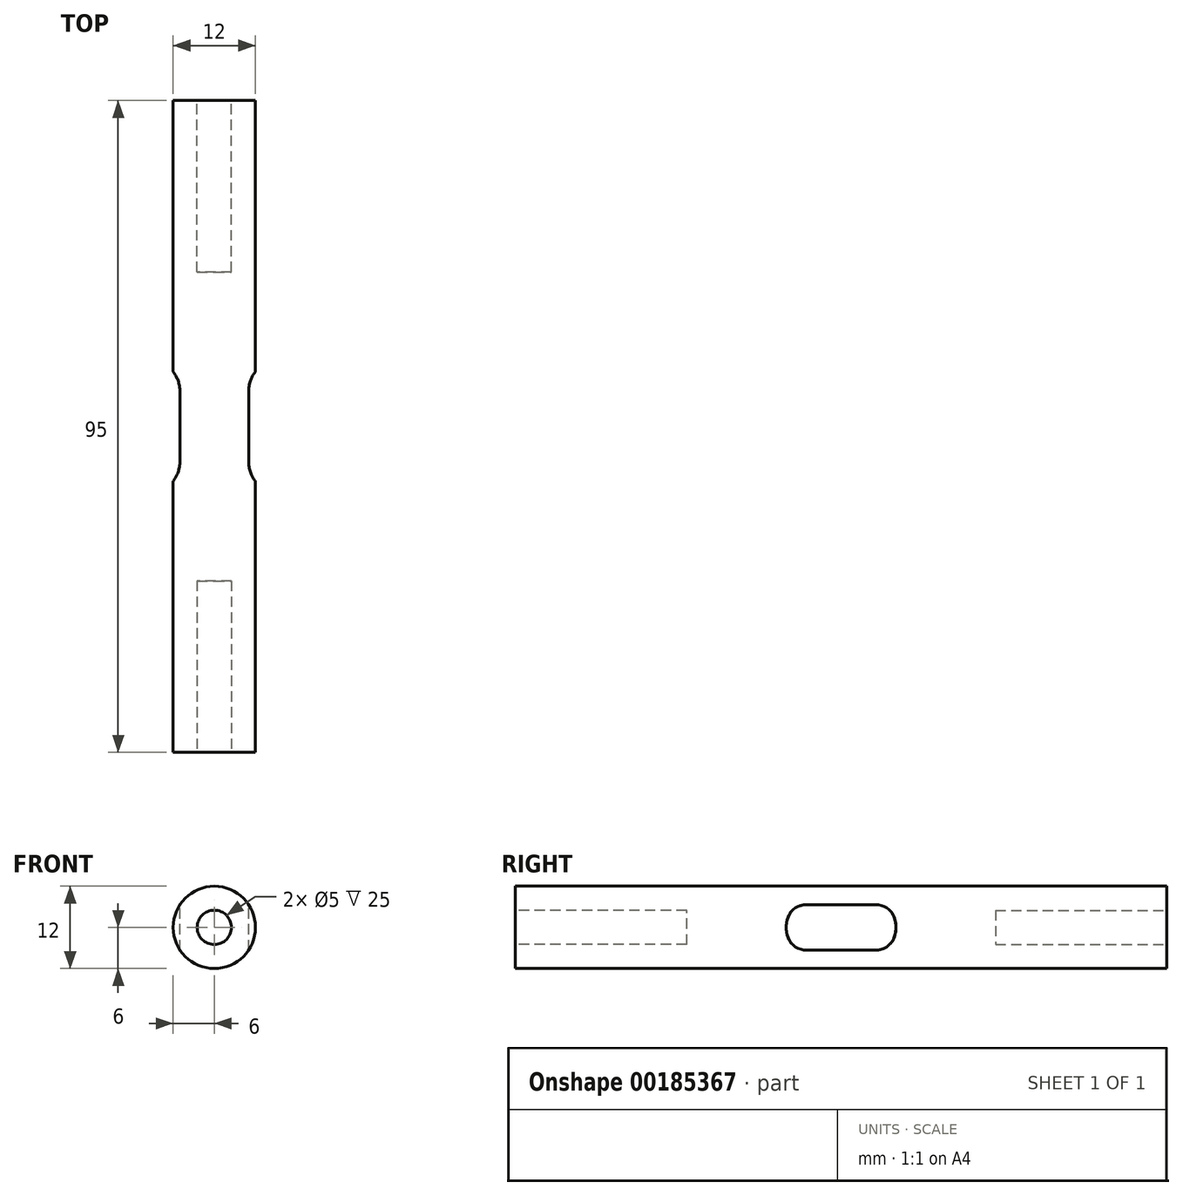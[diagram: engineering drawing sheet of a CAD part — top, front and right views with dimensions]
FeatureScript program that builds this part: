
annotation { "Feature Type Name" : "Feature", "Feature Type Description" : "" }
export const myFeature = defineFeature(function(context is Context, id is Id, definition is map)
    precondition{}
    {
        {
            var Q0;
            Q0=qCreatedBy(makeId("Front.planeOp"),FACE);
            var sketch = newSketch(context, id + "F0", { "sketchPlane" : qUnion([Q0])});
            skCircle(sketch, "E0", {"center": v(0, 0) * mm, "radius": 6 * mm});
            skSolve(sketch);
        }
        {
            var Q0;
            Q0=makeQuery(id+"F0.imprint","IMPRINT",FACE,{"disambiguationData":[TD([[makeQuery(id+"F0.imprint","IMPRINT",EDGE,{"derivedFrom":sQuery(id+"F0.wireOp",EDGE,"E0")}),1.0]])]});
            extrude(context, id + "F1", {"entities" : qUnion([Q0]), "depth" : 95 * mm});
        }
        {
            var Q0;
            Q0=makeQuery(id+"F1.opExtrude","CAP_FACE",FACE,{"disambiguationData":[OSD([sQuery(id+"F0.wireOp",EDGE,"E0")])],"isStart":true});
            var sketch = newSketch(context, id + "F2", { "sketchPlane" : qUnion([Q0])});
            skCircle(sketch, "E1", {"center": v(0, 0) * mm, "radius": 2.5 * mm});
            skSolve(sketch);
        }
        {
            var Q0;
            Q0=makeQuery(id+"F2.imprint","IMPRINT",FACE,{"disambiguationData":[TD([[makeQuery(id+"F2.imprint","IMPRINT",EDGE,{"derivedFrom":sQuery(id+"F2.wireOp",EDGE,"E1")}),1.0]])]});
            extrude(context, id + "F3", {"entities" : qUnion([Q0]), "operationType" : NewBodyOperationType.REMOVE, "oppositeDirection" : true, "depth" : 25 * mm});
        }
        {
            var Q0;
            Q0=makeQuery(id+"F1.opExtrude","CAP_FACE",FACE,{"disambiguationData":[OSD([sQuery(id+"F0.wireOp",EDGE,"E0")])],"isStart":false});
            var sketch = newSketch(context, id + "F4", { "sketchPlane" : qUnion([Q0])});
            skCircle(sketch, "E2", {"center": v(0, 0) * mm, "radius": 2.5 * mm});
            skSolve(sketch);
        }
        {
            var Q0;
            Q0=makeQuery(id+"F4.imprint","IMPRINT",FACE,{"disambiguationData":[TD([[makeQuery(id+"F4.imprint","IMPRINT",EDGE,{"derivedFrom":sQuery(id+"F4.wireOp",EDGE,"E2")}),1.0]])]});
            extrude(context, id + "F5", {"entities" : qUnion([Q0]), "operationType" : NewBodyOperationType.REMOVE, "oppositeDirection" : true, "depth" : 25 * mm});
        }
        {
            var Q0;
            Q0=qCreatedBy(makeId("Top.planeOp"),FACE);
            var sketch = newSketch(context, id + "F6", { "sketchPlane" : qUnion([Q0])});
            skLineSegment(sketch, "E3.bottom", {"start": v(10, -37.5) * mm, "end": v(11.65, -37.5) * mm});
            skLineSegment(sketch, "E3.top", {"start": v(10, -57.5) * mm, "end": v(11.65, -57.5) * mm});
            skLineSegment(sketch, "E3.left", {"start": v(5, -42.5) * mm, "end": v(5, -52.5) * mm});
            skLineSegment(sketch, "E3.right", {"start": v(11.65, -37.5) * mm, "end": v(11.65, -57.5) * mm});
            skPoint(sketch, "E4.visualSharp", {"position": v(5, -37.5) * mm});
            skArc(sketch, "E4.filletArc", {"start": v(10, -37.5) * mm, "mid": v(6.46, -38.96) * mm, "end": v(5, -42.5) * mm});
            skPoint(sketch, "E5.visualSharp", {"position": v(5, -57.5) * mm});
            skArc(sketch, "E5.filletArc", {"start": v(5, -52.5) * mm, "mid": v(6.46, -56.04) * mm, "end": v(10, -57.5) * mm});
            skLineSegment(sketch, "E6.MirrorCS", {"start": v(-10, -37.5) * mm, "end": v(-11.65, -37.5) * mm});
            skLineSegment(sketch, "E7.MirrorCS", {"start": v(-10, -57.5) * mm, "end": v(-11.65, -57.5) * mm});
            skArc(sketch, "E8.MirrorCS", {"start": v(-5, -52.5) * mm, "mid": v(-6.46, -56.04) * mm, "end": v(-10, -57.5) * mm});
            skPoint(sketch, "E9.MirrorP", {"position": v(-5, -57.5) * mm});
            skLineSegment(sketch, "E10.MirrorCS", {"start": v(-11.65, -37.5) * mm, "end": v(-11.65, -57.5) * mm});
            skLineSegment(sketch, "E11.MirrorCS", {"start": v(-5, -42.5) * mm, "end": v(-5, -52.5) * mm});
            skArc(sketch, "E12.MirrorCS", {"start": v(-10, -37.5) * mm, "mid": v(-6.46, -38.96) * mm, "end": v(-5, -42.5) * mm});
            skPoint(sketch, "E13.MirrorP", {"position": v(-5, -37.5) * mm});
            skSolve(sketch);
        }
        {
            var Q0;
            Q0=makeQuery(id+"F6.imprint","IMPRINT",FACE,{"disambiguationData":[TD([[makeQuery(id+"F6.imprint","IMPRINT",EDGE,{"derivedFrom":sQuery(id+"F6.wireOp",EDGE,"E3.bottom")}),-1.0]])]});
            var Q1;
            Q1=makeQuery(id+"F6.imprint","IMPRINT",FACE,{"disambiguationData":[TD([[makeQuery(id+"F6.imprint","IMPRINT",EDGE,{"derivedFrom":sQuery(id+"F6.wireOp",EDGE,"E6.MirrorCS")}),1.0]])]});
            extrude(context, id + "F7", {"entities" : qUnion([Q0, Q1]), "operationType" : NewBodyOperationType.REMOVE, "endBound" : BoundingType.SYMMETRIC, "oppositeDirection" : true, "depth" : 25 * mm});
        }
    });
